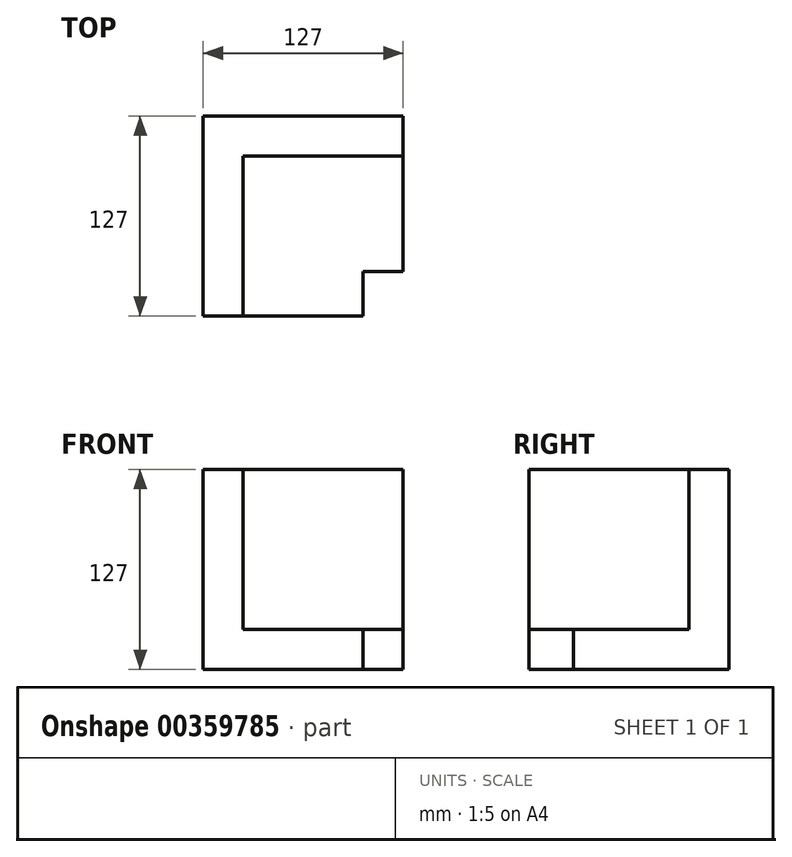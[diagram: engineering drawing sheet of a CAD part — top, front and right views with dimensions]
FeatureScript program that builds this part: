
annotation { "Feature Type Name" : "Feature", "Feature Type Description" : "" }
export const myFeature = defineFeature(function(context is Context, id is Id, definition is map)
    precondition{}
    {
        {
            var Q0;
            Q0=qCreatedBy(makeId("Front.planeOp"),FACE);
            var sketch = newSketch(context, id + "F0", { "sketchPlane" : qUnion([Q0])});
            skLineSegment(sketch, "E0.bottom", {"start": v(0, 0) * mm, "end": v(127, 0) * mm});
            skLineSegment(sketch, "E0.top", {"start": v(0, -127) * mm, "end": v(127, -127) * mm});
            skLineSegment(sketch, "E0.left", {"start": v(0, 0) * mm, "end": v(0, -127) * mm});
            skLineSegment(sketch, "E0.right", {"start": v(127, 0) * mm, "end": v(127, -127) * mm});
            skSolve(sketch);
        }
        {
            var Q0;
            Q0 = qSketchRegion(id + "F0", true);
            extrude(context, id + "F1", {"entities" : qUnion([Q0]), "depth" : 127 * mm});
        }
        {
            var Q0;
            Q0=makeQuery(id+"F1.opExtrude","SWEPT_FACE",FACE,{"disambiguationData":[OSD([sQuery(id+"F0.wireOp",EDGE,"E0.bottom")])]});
            var sketch = newSketch(context, id + "F2", { "sketchPlane" : qUnion([Q0])});
            skLineSegment(sketch, "E1.bottom", {"start": v(127, -127) * mm, "end": v(101.6, -127) * mm});
            skLineSegment(sketch, "E1.top", {"start": v(127, -98.73) * mm, "end": v(101.6, -98.73) * mm});
            skLineSegment(sketch, "E1.left", {"start": v(127, -127) * mm, "end": v(127, -98.73) * mm});
            skLineSegment(sketch, "E1.right", {"start": v(101.6, -127) * mm, "end": v(101.6, -98.73) * mm});
            skSolve(sketch);
        }
        {
            var Q0;
            Q0 = qSketchRegion(id + "FdIiproNy1qpxt3_1", true);
            var Q1;
            Q1=makeQuery(id+"F2.imprint","IMPRINT",FACE,{"disambiguationData":[TD([[makeQuery(id+"F2.imprint","IMPRINT",EDGE,{"derivedFrom":sQuery(id+"F2.wireOp",EDGE,"E1.bottom")}),1.0]])]});
            extrude(context, id + "F3", {"entities" : qUnion([Q0, Q1]), "operationType" : NewBodyOperationType.REMOVE, "oppositeDirection" : true, "depth" : 127 * mm});
        }
        {
            var Q0;
            Q0=makeQuery(id+"F1.opExtrude","SWEPT_FACE",FACE,{"disambiguationData":[OSD([sQuery(id+"F0.wireOp",EDGE,"E0.bottom")])]});
            var sketch = newSketch(context, id + "F4", { "sketchPlane" : qUnion([Q0])});
            skLineSegment(sketch, "E2", {"start": v(25.4, -127) * mm, "end": v(25.4, -25.4) * mm});
            skLineSegment(sketch, "E3", {"start": v(25.4, -25.4) * mm, "end": v(127, -25.4) * mm});
            skSolve(sketch);
        }
        {
            var Q0;
            Q0 = qSketchRegion(id + "FhbUmam5nYsVH2D_1", true);
            var Q1;
            {var subQ3=sQuery(id+"F4.wireOp",EDGE,"E2");Q1=makeQuery(id+"F4.imprint","IMPRINT",FACE,{"disambiguationData":[TD([[makeQuery(id+"F4.imprint","IMPRINT",EDGE,{"derivedFrom":subQ3}),-1.0]])]});}
            extrude(context, id + "F5", {"entities" : qUnion([Q0, Q1]), "operationType" : NewBodyOperationType.REMOVE, "oppositeDirection" : true, "depth" : 101.6 * mm});
        }
    });
